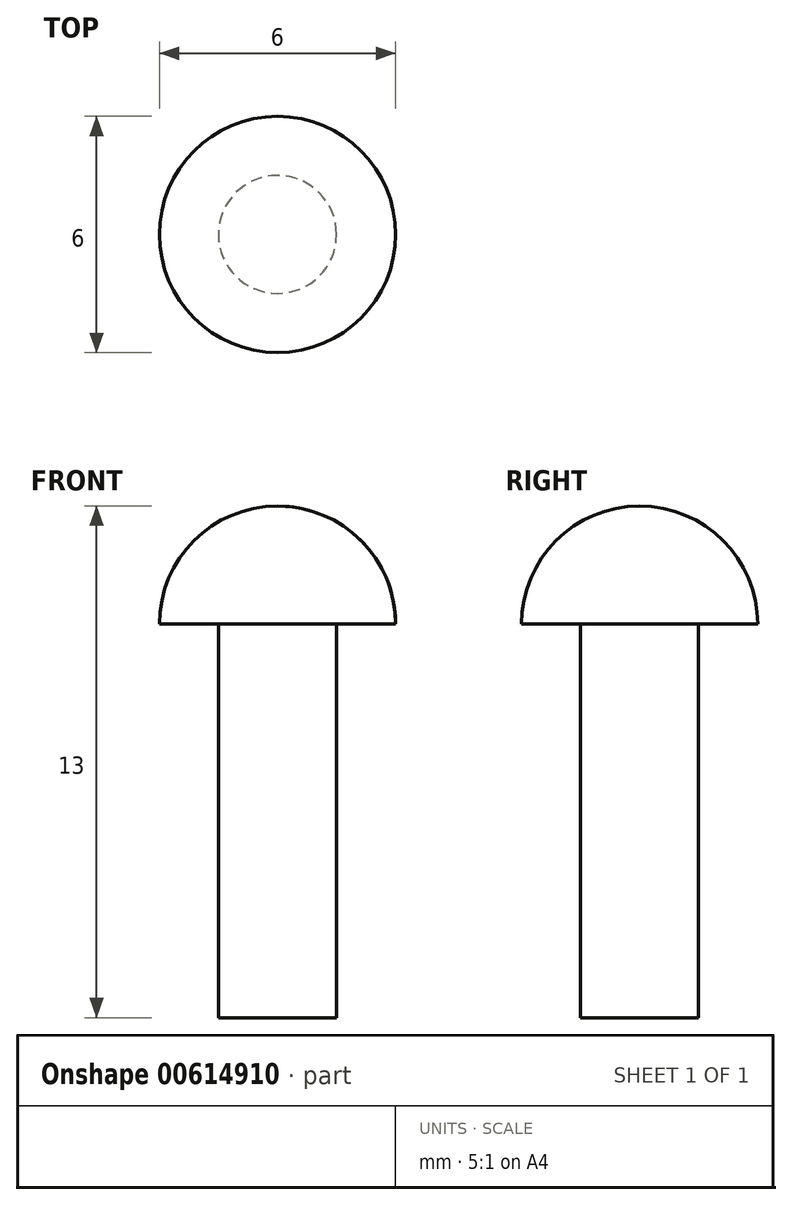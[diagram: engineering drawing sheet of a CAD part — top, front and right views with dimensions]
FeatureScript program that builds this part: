
annotation { "Feature Type Name" : "Feature", "Feature Type Description" : "" }
export const myFeature = defineFeature(function(context is Context, id is Id, definition is map)
    precondition{}
    {
        {
            var Q0;
            Q0=qCreatedBy(makeId("Top.planeOp"),FACE);
            var sketch = newSketch(context, id + "F0", { "sketchPlane" : qUnion([Q0])});
            skCircle(sketch, "E0", {"center": v(0, 0) * mm, "radius": 1.5 * mm});
            skSolve(sketch);
        }
        {
            var Q0;
            Q0 = qSketchRegion(id + "F0", true);
            extrude(context, id + "F1", {"entities" : qUnion([Q0]), "oppositeDirection" : true, "depth" : 10 * mm, "offsetDistance" : 25 * mm});
        }
        {
            var Q0;
            Q0=qCreatedBy(makeId("Front.planeOp"),FACE);
            var sketch = newSketch(context, id + "F2", { "sketchPlane" : qUnion([Q0])});
            skArc(sketch, "E1", {"start": v(3, 0) * mm, "mid": v(2.12, 2.12) * mm, "end": v(0, 3) * mm});
            skLineSegment(sketch, "E2", {"start": v(3, 0) * mm, "end": v(0, 0) * mm});
            skLineSegment(sketch, "E3", {"start": v(0, 3) * mm, "end": v(0, 0) * mm});
            skSolve(sketch);
        }
        {
            var Q0;
            Q0=makeQuery(id+"F2.imprint","IMPRINT",FACE,{"disambiguationData":[TD([[makeQuery(id+"F2.imprint","IMPRINT",EDGE,{"derivedFrom":sQuery(id+"F2.wireOp",EDGE,"E1")}),1.0]])]});
            var Q1;
            Q1=sQuery(id+"F2.wireOp",EDGE,"E3");
            revolve(context, id + "F3", {"operationType" : NewBodyOperationType.ADD, "entities" : qUnion([Q0]), "axis" : qUnion([Q1]), "revolveType" : RevolveType.FULL});
        }
    });
